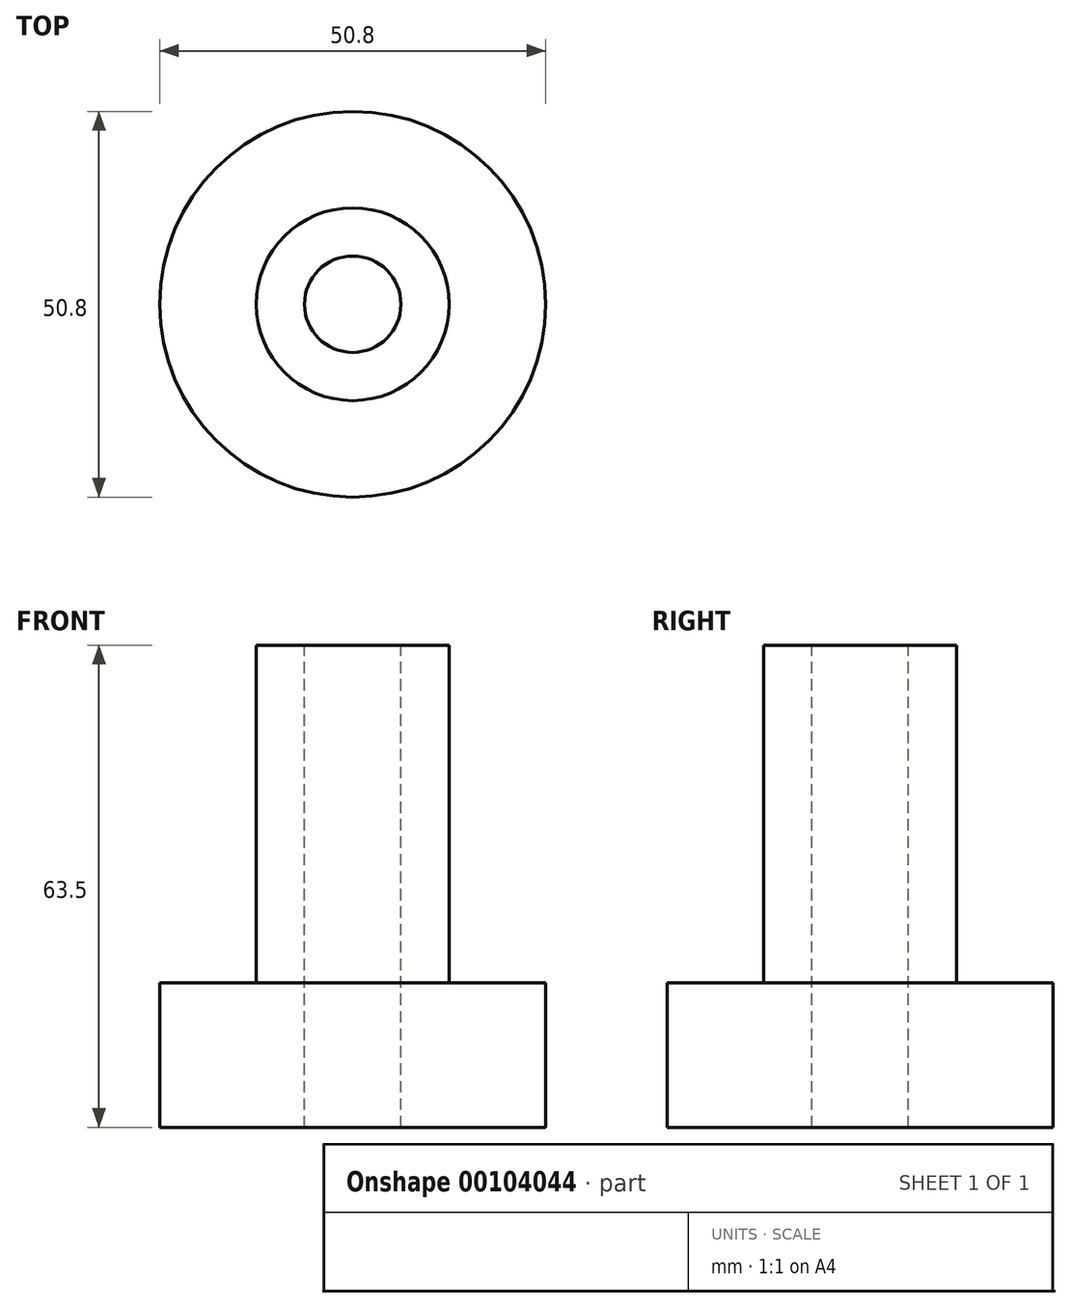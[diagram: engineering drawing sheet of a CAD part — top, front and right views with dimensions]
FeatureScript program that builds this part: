
annotation { "Feature Type Name" : "Feature", "Feature Type Description" : "" }
export const myFeature = defineFeature(function(context is Context, id is Id, definition is map)
    precondition{}
    {
        {
            var Q0;
            Q0=qCreatedBy(makeId("Top.planeOp"),FACE);
            var sketch = newSketch(context, id + "F0", { "sketchPlane" : qUnion([Q0])});
            skCircle(sketch, "E0", {"center": v(0, 0) * mm, "radius": 25.4 * mm});
            skSolve(sketch);
        }
        {
            var Q0;
            Q0 = qSketchRegion(id + "F0", true);
            extrude(context, id + "F1", {"entities" : qUnion([Q0]), "depth" : 19.05 * mm});
        }
        {
            var Q0;
            Q0=makeQuery(id+"F1.opExtrude","CAP_FACE",FACE,{"disambiguationData":[OSD([sQuery(id+"F0.wireOp",EDGE,"E0")])],"isStart":false});
            var sketch = newSketch(context, id + "F2", { "sketchPlane" : qUnion([Q0])});
            skCircle(sketch, "E1", {"center": v(0, 0) * mm, "radius": 12.7 * mm});
            skSolve(sketch);
        }
        {
            var Q0;
            Q0 = qSketchRegion(id + "F2", true);
            extrude(context, id + "F3", {"entities" : qUnion([Q0]), "operationType" : NewBodyOperationType.ADD, "depth" : 44.45 * mm});
        }
        {
            var Q0;
            Q0=makeQuery(id+"F3.opExtrude","CAP_FACE",FACE,{"disambiguationData":[OSD([sQuery(id+"F2.wireOp",EDGE,"E1")])],"isStart":false});
            var sketch = newSketch(context, id + "F4", { "sketchPlane" : qUnion([Q0])});
            skCircle(sketch, "E2", {"center": v(0, 0) * mm, "radius": 6.35 * mm});
            skSolve(sketch);
        }
        {
            var Q0;
            Q0 = qSketchRegion(id + "F4", true);
            extrude(context, id + "F5", {"entities" : qUnion([Q0]), "operationType" : NewBodyOperationType.REMOVE, "endBound" : BoundingType.THROUGH_ALL, "oppositeDirection" : true, "depth" : 25.4 * mm});
        }
    });
